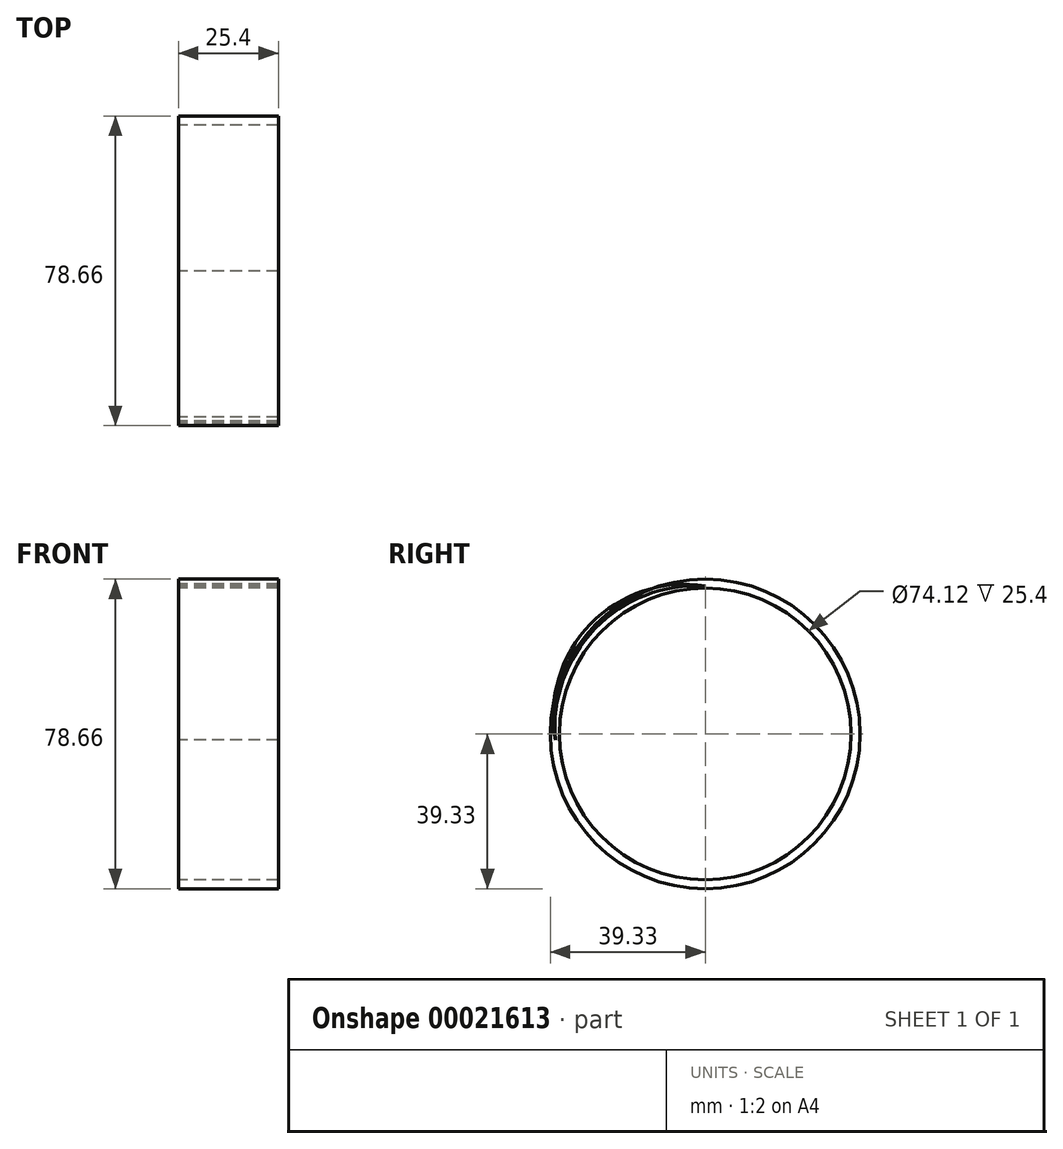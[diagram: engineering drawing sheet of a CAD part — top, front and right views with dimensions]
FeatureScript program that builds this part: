
annotation { "Feature Type Name" : "Feature", "Feature Type Description" : "" }
export const myFeature = defineFeature(function(context is Context, id is Id, definition is map)
    precondition{}
    {
        {
            var Q0;
            Q0=qCreatedBy(makeId("Right.planeOp"),FACE);
            var sketch = newSketch(context, id + "F0", { "sketchPlane" : qUnion([Q0])});
            skCircle(sketch, "E0", {"center": v(0, 0) * mm, "radius": 37.06 * mm});
            skCircle(sketch, "E1", {"center": v(0, 0) * mm, "radius": 39.33 * mm});
            skSolve(sketch);
        }
        {
            var Q0;
            Q0 = qSketchRegion(id + "F0", true);
            extrude(context, id + "F1", {"entities" : qUnion([Q0]), "depth" : 25.4 * mm});
        }
        {
            var Q0;
            Q0=qCreatedBy(makeId("Right.planeOp"),FACE);
            var sketch = newSketch(context, id + "F2", { "sketchPlane" : qUnion([Q0])});
            skLineSegment(sketch, "E2", {"start": v(0.37, 38.13) * mm, "end": v(0, 37.66) * mm});
            skLineSegment(sketch, "E3", {"start": v(-36.22, -7.92) * mm, "end": v(-36.75, -8.6) * mm});
            skArc(sketch, "E4", {"start": v(0, 37.66) * mm, "mid": v(-30.36, 24.05) * mm, "end": v(-36.75, -8.6) * mm});
            skArc(sketch, "E5", {"start": v(0, 37.66) * mm, "mid": v(-31.37, 25.4) * mm, "end": v(-36.22, -7.92) * mm});
            skSolve(sketch);
        }
        {
            var Q0;
            Q0=makeQuery(id+"F2.imprint","IMPRINT",FACE,{"disambiguationData":[TD([[makeQuery(id+"F2.imprint","IMPRINT",EDGE,{"derivedFrom":sQuery(id+"F2.wireOp",EDGE,"E4")}),-1.0]])]});
            extrude(context, id + "F3", {"entities" : qUnion([Q0]), "depth" : 25.4 * mm});
        }
    });
